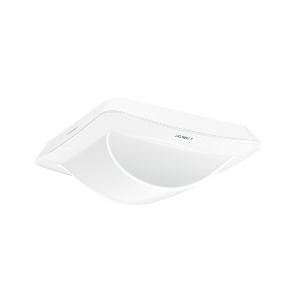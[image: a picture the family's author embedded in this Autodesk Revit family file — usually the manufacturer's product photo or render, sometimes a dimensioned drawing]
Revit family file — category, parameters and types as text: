
# Revit family: hallway_058036
name_source: partatom
category: Elektroinstallationen
revit_build: Autodesk Revit 2016 (Build: 20190508_0715(x64)
units: mm (PartAtom-declared; Revit-internal decimal feet)

## family parameters
Basisbauteil = Fläche
Beim Laden mit Abzugskörper schneiden = Nein
Bemaßung runder Anschluss = Durchmesser verwenden
Beschriftungsausrichtung beibehalten = Nein
Gemeinsam genutzt = Nein
Raumberechnungspunkt = Nein
Teiletyp = Normal

## types (1)
- Hallway
    Apparent Load = 0 VA
    Beschreibung = Type: Presence detector; Dimensions (L x W x H): 67 x 103 x 103 mm; Mains power supply: 30 V; Power consumption: 0,7 W; Power supply, detail: KNX bus; Sensor Technology: High frequency; Application, place: Indoors; Application, room: Indoors, corridor / aisle; Installation site: ceiling; Installation: Concealed wiring; HF-system: 5,8 GHz; Electronic scalability: Yes; Mechanical scalability: No; Mounting height: 2 – 4 m; Optimum mounting height: 2,8 m; Detection: also through glass, wood and stud walls; Detection angle: 360 °; Angle of aperture: 160 °; Sneak-by guard: Yes; Capability of masking out individual segments: No; Reach, radial: 25 x 3 m (75 m²); Reach, tangential: 25 x 3 m (75 m²); Twilight setting TEACH: Yes; Twilight setting: 2 – 1000 lx; Time setting: 10 sec – 1092 min; Constant-lighting control: Yes; Basic light level function: Yes; KNX functions: Comfort, Photo-cell controller, Individual pyro evaluation, Basic light level function, Light level, HVAC output, Constant-lighting control, Light output 4x, Presence output, Day / night function, Dewpoint; With bus coupling: Yes; Settings via: ETS software, Bluetooth, Bus; With remote control: No; Interconnection: Yes; IP-rating: IP20; Material: Plastic; Ambient temperature: -25 – 50 °C; Colour: white; Colour, RAL: 9010; Manufacturer's Warranty: 5 years; Version: KNX - Concealed wiring; PU1, EAN: 4007841058036
    Height = 0 mm  [stored 0 ft]
    Hersteller = Steinel
    Length = 67 mm
    Maximum range = 10.635 m
    ModVariant = Nein
    Modell = 058036
    Mounting Place = Ceiling
    Mounting Type = Recessed
    Number of Poles = 1
    OnlyDefault = Ja
    Power Factor = 1
    Product Name = Hallway
    Product group = Presence detector
    ProductGroupID = 4
    Protection Class = Protection class
    Protection Degree = IP 20
    RlxData = <blob elided: 187681 chars, md5=47c00e7b>
    Sensor characteristics = Stretched
    Sensor type = HF
    SensorDataFile = <blob elided: 184606 chars, md5=d44d1097>
    Type of entry = Motion
    Typenbild = produkt1_058036.jpg
    Typenkommentare = Product without accessories
    URL = http://relux.com
    VarID = ---
    Voltage = 0 V
    Vorgabe-Ansicht = 1800 mm
    Weight = 0.00 kg
    Width = 103 mm

note: [stored X ft] marks values corroborated as IEEE doubles in the binary element streams (Revit-internal decimal feet)

## geometry (parser evidence)
native form markers: Blend x4, Sweep x14
no freeform markers — native parametric forms only
